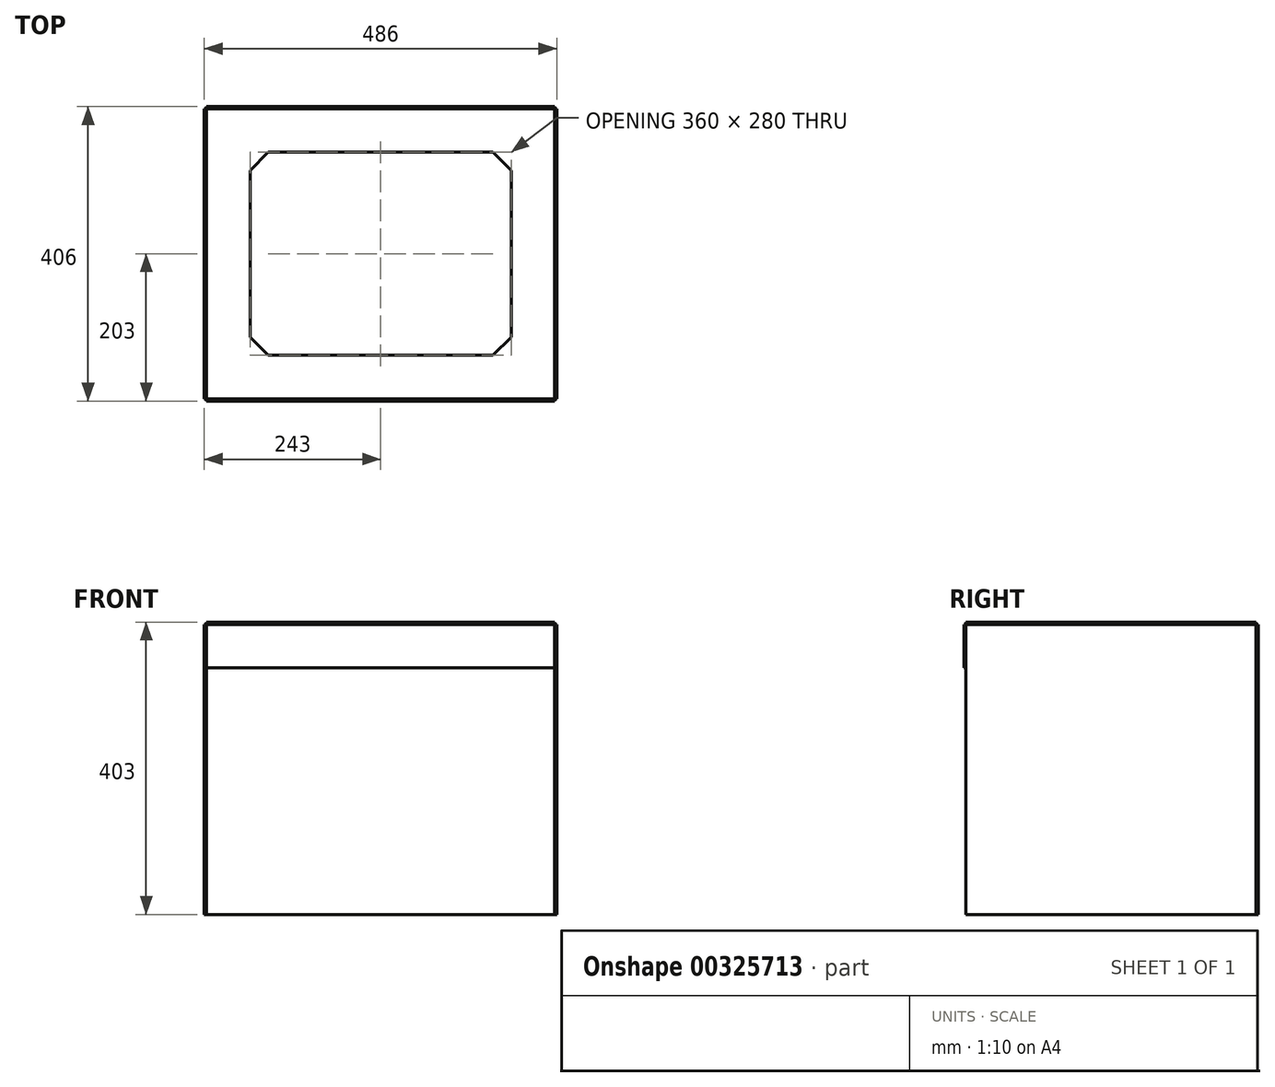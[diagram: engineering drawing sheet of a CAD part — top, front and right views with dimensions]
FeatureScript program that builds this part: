
annotation { "Feature Type Name" : "Feature", "Feature Type Description" : "" }
export const myFeature = defineFeature(function(context is Context, id is Id, definition is map)
    precondition{}
    {
        {
            assignVariable(context, id + "F0", {"name" : "ESPESOR", "anyValue" : 3});
        }
        {
            assignVariable(context, id + "F1", {"name" : "CHAFLAN_VENTANA", "anyValue" : 25});
        }
        {
            var Q0;
            Q0=qCreatedBy(makeId("Front.planeOp"),FACE);
            var sketch = newSketch(context, id + "F2", { "sketchPlane" : qUnion([Q0])});
            skPoint(sketch, "E0", {"position": v(0, 400) * mm});
            skSolve(sketch);
        }
        {
            var Q0;
            Q0=sQuery(id+"F2.wireOp",VERTEX,"E0");
            var Q1;
            Q1=qCreatedBy(makeId("Top.planeOp"),FACE);
            cPlane(context, id + "F3", {"entities" : qUnion([Q0, Q1]), "cplaneType" : CPlaneType.PLANE_POINT, "offset" : 25 * mm, "width" : 150 * mm, "height" : 150 * mm});
        }
        {
            var Q0;
            Q0=qCreatedBy(id+"F3.planeOp",FACE);
            var sketch = newSketch(context, id + "F4", { "sketchPlane" : qUnion([Q0])});
            skLineSegment(sketch, "E1.bottom", {"start": v(240, 200) * mm, "end": v(-240, 200) * mm});
            skLineSegment(sketch, "E1.top", {"start": v(240, -200) * mm, "end": v(-240, -200) * mm});
            skLineSegment(sketch, "E1.left", {"start": v(240, 200) * mm, "end": v(240, -200) * mm});
            skLineSegment(sketch, "E1.right", {"start": v(-240, 200) * mm, "end": v(-240, -200) * mm});
            skPoint(sketch, "E1.middle", {"position": v(0, 0) * mm});
            skLineSegment(sketch, "E2.bottom", {"start": v(180, 140) * mm, "end": v(-180, 140) * mm});
            skLineSegment(sketch, "E2.top", {"start": v(180, -140) * mm, "end": v(-180, -140) * mm});
            skLineSegment(sketch, "E2.left", {"start": v(180, 140) * mm, "end": v(180, -140) * mm});
            skLineSegment(sketch, "E2.right", {"start": v(-180, 140) * mm, "end": v(-180, -140) * mm});
            skSolve(sketch);
        }
        {
            var Q0;
            Q0=qCreatedBy(makeId("Right.planeOp"),FACE);
            var Q1;
            Q1=sQuery(id+"F4.wireOp",VERTEX,"E1.right.end");
            cPlane(context, id + "F5", {"entities" : qUnion([Q0, Q1]), "cplaneType" : CPlaneType.PLANE_POINT, "offset" : 25 * mm, "width" : 150 * mm, "height" : 150 * mm});
        }
        {
            var Q0;
            Q0=qCreatedBy(id+"F5.planeOp",FACE);
            var sketch = newSketch(context, id + "F6", { "sketchPlane" : qUnion([Q0])});
            skLineSegment(sketch, "E3.bottom", {"start": v(-200, 400) * mm, "end": v(200, 400) * mm});
            skLineSegment(sketch, "E3.top", {"start": v(-200, 0) * mm, "end": v(200, 0) * mm});
            skLineSegment(sketch, "E3.left", {"start": v(-200, 400) * mm, "end": v(-200, 0) * mm});
            skLineSegment(sketch, "E3.right", {"start": v(200, 400) * mm, "end": v(200, 0) * mm});
            skSolve(sketch);
        }
        {
            var Q0;
            Q0=sQuery(id+"F4.wireOp",VERTEX,"E1.right.start");
            var Q1;
            Q1=qCreatedBy(makeId("Front.planeOp"),FACE);
            cPlane(context, id + "F7", {"entities" : qUnion([Q0, Q1]), "cplaneType" : CPlaneType.PLANE_POINT, "offset" : 25 * mm, "width" : 150 * mm, "height" : 150 * mm});
        }
        {
            var Q0;
            Q0=qCreatedBy(id+"F7.planeOp",FACE);
            var sketch = newSketch(context, id + "F8", { "sketchPlane" : qUnion([Q0])});
            skLineSegment(sketch, "E4.bottom", {"start": v(-240, 400) * mm, "end": v(240, 400) * mm});
            skLineSegment(sketch, "E4.top", {"start": v(-240, 0) * mm, "end": v(240, 0) * mm});
            skLineSegment(sketch, "E4.left", {"start": v(-240, 400) * mm, "end": v(-240, 0) * mm});
            skLineSegment(sketch, "E4.right", {"start": v(240, 400) * mm, "end": v(240, 0) * mm});
            skSolve(sketch);
        }
        {
            var Q0;
            Q0=sQuery(id+"F4.wireOp",VERTEX,"E1.left.end");
            var Q1;
            Q1=qCreatedBy(makeId("Right.planeOp"),FACE);
            cPlane(context, id + "F9", {"entities" : qUnion([Q0, Q1]), "cplaneType" : CPlaneType.PLANE_POINT, "offset" : 25 * mm, "width" : 150 * mm, "height" : 150 * mm});
        }
        {
            var Q0;
            Q0=qCreatedBy(id+"F9.planeOp",FACE);
            var sketch = newSketch(context, id + "F10", { "sketchPlane" : qUnion([Q0])});
            skLineSegment(sketch, "E5.bottom", {"start": v(200, 400) * mm, "end": v(-200, 400) * mm});
            skLineSegment(sketch, "E5.top", {"start": v(200, 0) * mm, "end": v(-200, 0) * mm});
            skLineSegment(sketch, "E5.left", {"start": v(200, 400) * mm, "end": v(200, 0) * mm});
            skLineSegment(sketch, "E5.right", {"start": v(-200, 400) * mm, "end": v(-200, 0) * mm});
            skSolve(sketch);
        }
        {
            var Q0;
            Q0=sQuery(id+"F4.wireOp",VERTEX,"E1.right.end");
            var Q1;
            Q1=qCreatedBy(makeId("Front.planeOp"),FACE);
            cPlane(context, id + "F11", {"entities" : qUnion([Q0, Q1]), "cplaneType" : CPlaneType.PLANE_POINT, "offset" : 25 * mm, "width" : 150 * mm, "height" : 150 * mm});
        }
        {
            var Q0;
            Q0=qCreatedBy(id+"F11.planeOp",FACE);
            var sketch = newSketch(context, id + "F12", { "sketchPlane" : qUnion([Q0])});
            skLineSegment(sketch, "E6.bottom", {"start": v(-240, 400) * mm, "end": v(240, 400) * mm});
            skLineSegment(sketch, "E6.top", {"start": v(-240, 340) * mm, "end": v(240, 340) * mm});
            skLineSegment(sketch, "E6.left", {"start": v(-240, 400) * mm, "end": v(-240, 340) * mm});
            skLineSegment(sketch, "E6.right", {"start": v(240, 400) * mm, "end": v(240, 340) * mm});
            skSolve(sketch);
        }
        {
            var Q0;
            Q0=makeQuery(id+"F4.imprint","IMPRINT",FACE,{"disambiguationData":[TD([[makeQuery(id+"F4.imprint","IMPRINT",EDGE,{"derivedFrom":sQuery(id+"F4.wireOp",EDGE,"E1.bottom")}),1.0]])]});
            var Q1;
            Q1=sQuery(id+"F4.wireOp",EDGE,"E2.top");
            extrude(context, id + "F13", {"entities" : qUnion([Q0]), "surfaceEntities" : qUnion([Q1]), "depth" : (getVariable(context, 'ESPESOR')) * mm});
        }
        {
            var Q0;
            Q0=makeQuery(id+"F13.opExtrude","SWEPT_EDGE",EDGE,{"disambiguationData":[OSD([sQuery(id+"F4.wireOp",EDGE,"E2.top"),sQuery(id+"F4.wireOp",EDGE,"E2.right")])]});
            var Q1;
            Q1=makeQuery(id+"F13.opExtrude","SWEPT_EDGE",EDGE,{"disambiguationData":[OSD([sQuery(id+"F4.wireOp",EDGE,"E2.bottom"),sQuery(id+"F4.wireOp",EDGE,"E2.right")])]});
            var Q2;
            Q2=makeQuery(id+"F13.opExtrude","SWEPT_EDGE",EDGE,{"disambiguationData":[OSD([sQuery(id+"F4.wireOp",EDGE,"E2.bottom"),sQuery(id+"F4.wireOp",EDGE,"E2.left")])]});
            var Q3;
            Q3=makeQuery(id+"F13.opExtrude","SWEPT_EDGE",EDGE,{"disambiguationData":[OSD([sQuery(id+"F4.wireOp",EDGE,"E2.top"),sQuery(id+"F4.wireOp",EDGE,"E2.left")])]});
            chamfer(context, id + "F14", {"entities" : qUnion([Q0, Q1, Q2, Q3]), "width" : (getVariable(context, 'CHAFLAN_VENTANA')) * mm, "tangentPropagation" : true});
        }
        {
            var Q0;
            Q0=makeQuery(id+"F6.imprint","IMPRINT",FACE,{"disambiguationData":[TD([[makeQuery(id+"F6.imprint","IMPRINT",EDGE,{"derivedFrom":sQuery(id+"F6.wireOp",EDGE,"E3.bottom")}),-1.0]])]});
            extrude(context, id + "F15", {"entities" : qUnion([Q0]), "oppositeDirection" : true, "depth" : (getVariable(context, 'ESPESOR')) * mm});
        }
        {
            var Q0;
            Q0=makeQuery(id+"F10.imprint","IMPRINT",FACE,{"disambiguationData":[TD([[makeQuery(id+"F10.imprint","IMPRINT",EDGE,{"derivedFrom":sQuery(id+"F10.wireOp",EDGE,"E5.bottom")}),1.0]])]});
            extrude(context, id + "F16", {"entities" : qUnion([Q0]), "depth" : (getVariable(context, 'ESPESOR')) * mm});
        }
        {
            var Q0;
            Q0=makeQuery(id+"F8.imprint","IMPRINT",FACE,{"disambiguationData":[TD([[makeQuery(id+"F8.imprint","IMPRINT",EDGE,{"derivedFrom":sQuery(id+"F8.wireOp",EDGE,"E4.bottom")}),-1.0]])]});
            extrude(context, id + "F17", {"entities" : qUnion([Q0]), "oppositeDirection" : true, "depth" : (getVariable(context, 'ESPESOR')) * mm});
        }
        {
            var Q0;
            Q0 = qSketchRegion(id + "F12", true);
            extrude(context, id + "F18", {"entities" : qUnion([Q0]), "depth" : (getVariable(context, 'ESPESOR')) * mm});
        }
    });
